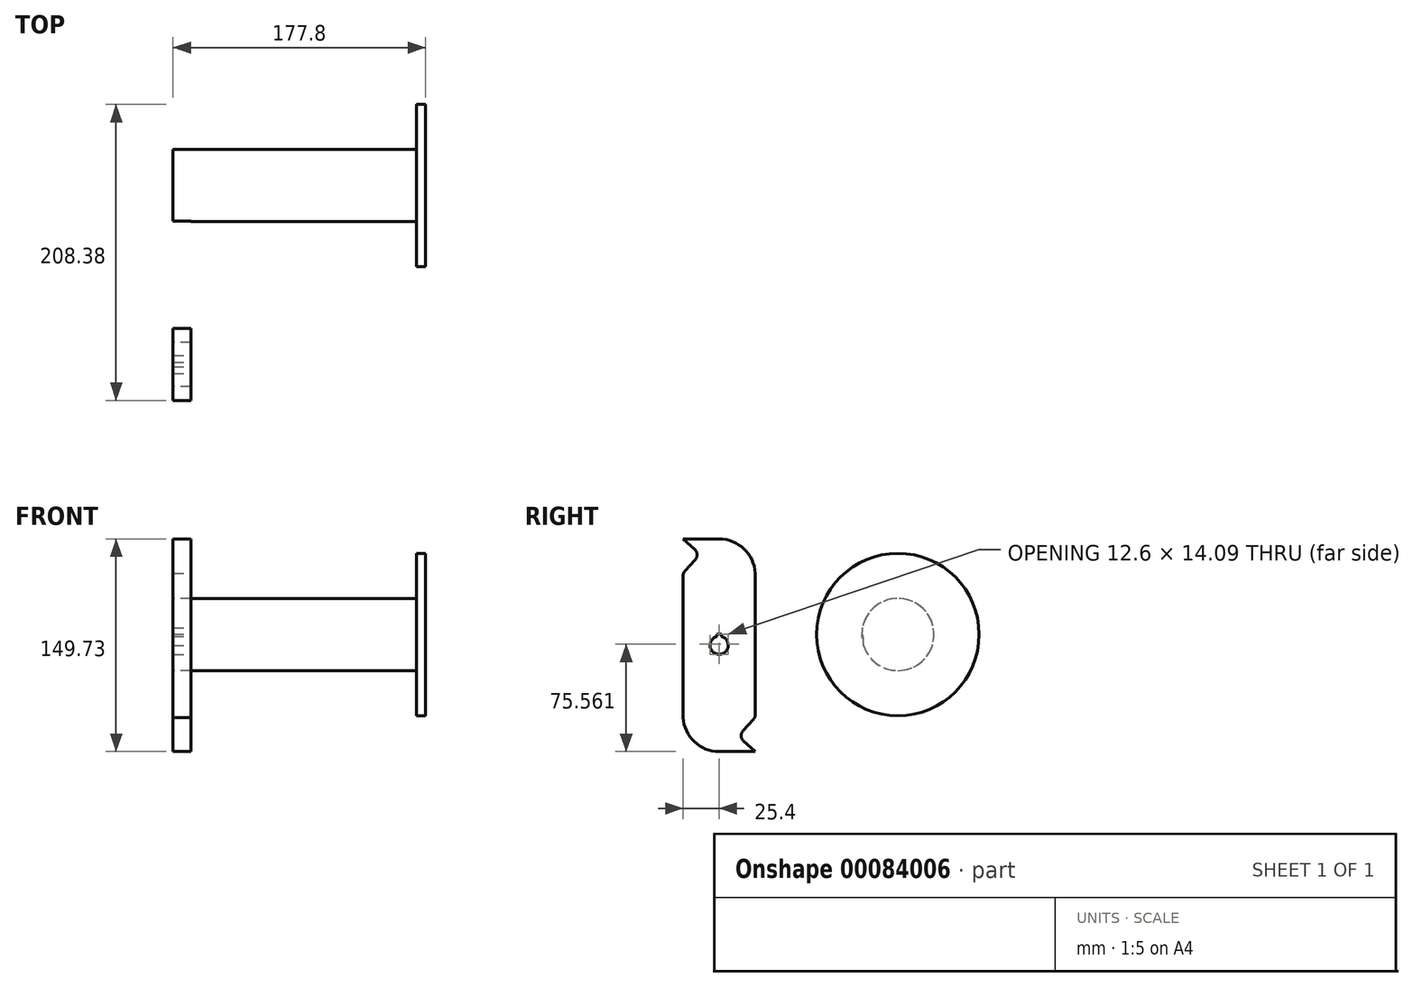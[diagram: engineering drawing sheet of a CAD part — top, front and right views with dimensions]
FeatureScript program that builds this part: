
annotation { "Feature Type Name" : "Feature", "Feature Type Description" : "" }
export const myFeature = defineFeature(function(context is Context, id is Id, definition is map)
    precondition{}
    {
        {
            var Q0;
            Q0=qCreatedBy(makeId("Right.planeOp"),FACE);
            var sketch = newSketch(context, id + "F0", { "sketchPlane" : qUnion([Q0])});
            skCircle(sketch, "E0", {"center": v(0, 0) * mm, "radius": 25.4 * mm});
            skSolve(sketch);
        }
        {
            var Q0;
            Q0=makeQuery(id+"F0.imprint","IMPRINT",FACE,{"disambiguationData":[TD([[makeQuery(id+"F0.imprint","IMPRINT",EDGE,{"derivedFrom":sQuery(id+"F0.wireOp",EDGE,"E0")}),1.0]])]});
            extrude(context, id + "F1", {"entities" : qUnion([Q0]), "depth" : 177.8 * mm});
        }
        {
            var Q0;
            Q0=makeQuery(id+"F1.opExtrude","CAP_FACE",FACE,{"disambiguationData":[OSD([sQuery(id+"F0.wireOp",EDGE,"E0")])],"isStart":false});
            var sketch = newSketch(context, id + "F2", { "sketchPlane" : qUnion([Q0])});
            skCircle(sketch, "E1", {"center": v(0, 0) * mm, "radius": 57.15 * mm});
            skSolve(sketch);
        }
        {
            var Q0;
            Q0=makeQuery(id+"F2.imprint","IMPRINT",FACE,{"disambiguationData":[TD([[makeQuery(id+"F2.imprint","IMPRINT",EDGE,{"derivedFrom":sQuery(id+"F2.wireOp",EDGE,"E1")}),1.0]])]});
            extrude(context, id + "F3", {"entities" : qUnion([Q0]), "operationType" : NewBodyOperationType.ADD, "oppositeDirection" : true, "depth" : 6.35 * mm});
        }
        {
            var Q0;
            Q0=qCreatedBy(makeId("Right.planeOp"),FACE);
            var sketch = newSketch(context, id + "F4", { "sketchPlane" : qUnion([Q0])});
            skCircle(sketch, "E2", {"center": v(-125.83, -7.6) * mm, "radius": 101.6 * mm});
            skSolve(sketch);
        }
        {
            var Q0;
            Q0=makeQuery(id+"F4.imprint","IMPRINT",FACE,{"disambiguationData":[TD([[makeQuery(id+"F4.imprint","IMPRINT",EDGE,{"derivedFrom":sQuery(id+"F4.wireOp",EDGE,"E2")}),1.0]])]});
            extrude(context, id + "F5", {"entities" : qUnion([Q0]), "depth" : 12.7 * mm});
        }
        {
            var Q0;
            Q0=makeQuery(id+"F5.opExtrude","CAP_FACE",FACE,{"disambiguationData":[OSD([sQuery(id+"F4.wireOp",EDGE,"E2")])],"isStart":false});
            var sketch = newSketch(context, id + "F6", { "sketchPlane" : qUnion([Q0])});
            skCircle(sketch, "E3", {"center": v(-125.83, -7.6) * mm, "radius": 6.35 * mm});
            skLineSegment(sketch, "E4", {"start": v(-127.42, -1.45) * mm, "end": v(-127.42, 0.13) * mm});
            skLineSegment(sketch, "E5", {"start": v(-127.42, 0.13) * mm, "end": v(-124.24, 0.13) * mm});
            skLineSegment(sketch, "E6", {"start": v(-124.24, 0.13) * mm, "end": v(-124.24, -1.45) * mm});
            skSolve(sketch);
        }
        {
            var Q0;
            {var subQ0=sQuery(id+"F6.wireOp",EDGE,"E3");var subQ1=makeQuery(id+"F6.imprint","INTERSECT",VERTEX,{"derivedFrom":[subQ0,sQuery(id+"F6.wireOp",EDGE,"E4")]});Q0=makeQuery(id+"F6.imprint","IMPRINT",FACE,{"disambiguationData":[TD([[makeQuery(id+"F6.imprint","IMPRINT",EDGE,{"disambiguationData":[TD([[subQ1,1.0]])],"derivedFrom":subQ0}),1.0]])]});}
            var Q1;
            {var subQ0=sQuery(id+"F6.wireOp",EDGE,"E4");Q1=makeQuery(id+"F6.imprint","IMPRINT",FACE,{"disambiguationData":[TD([[makeQuery(id+"F6.imprint","IMPRINT",EDGE,{"derivedFrom":subQ0}),-1.0]])]});}
            var Q2;
            Q2=makeQuery(id+"F5.opExtrude","CAP_FACE",FACE,{"disambiguationData":[OSD([sQuery(id+"F4.wireOp",EDGE,"E2")])],"isStart":true});
            var Q3;
            Q3=makeQuery(id+"F5.opExtrude","SWEPT_BODY",BODY,{"disambiguationData":[OSD([sQuery(id+"F4.wireOp",EDGE,"E2")])]});
            extrude(context, id + "F7", {"entities" : qUnion([Q0, Q1]), "operationType" : NewBodyOperationType.REMOVE, "endBound" : BoundingType.UP_TO_SURFACE, "oppositeDirection" : true, "endBoundEntityFace" : qUnion([Q2]), "endBoundEntityBody" : qUnion([Q3]), "depth" : 25.4 * mm});
        }
        {
            var Q0;
            Q0=makeQuery(id+"F5.opExtrude","CAP_FACE",FACE,{"disambiguationData":[OSD([sQuery(id+"F4.wireOp",EDGE,"E2")])],"isStart":false});
            var sketch = newSketch(context, id + "F8", { "sketchPlane" : qUnion([Q0])});
            skCircle(sketch, "E7", {"center": v(-125.83, -7.6) * mm, "radius": 25.4 * mm});
            skSolve(sketch);
        }
        {
            var Q0;
            Q0=makeQuery(id+"F8.imprint","IMPRINT",FACE,{"disambiguationData":[TD([[makeQuery(id+"F8.imprint","IMPRINT",EDGE,{"derivedFrom":sQuery(id+"F8.wireOp",EDGE,"E7")}),-1.0]])]});
            var sketch = newSketch(context, id + "F9", { "sketchPlane" : qUnion([Q0])});
            skLineSegment(sketch, "E8", {"start": v(-100.43, 43.2) * mm, "end": v(-100.43, -58.4) * mm});
            skLineSegment(sketch, "E9", {"start": v(-100.43, -58.4) * mm, "end": v(-151.23, -58.4) * mm});
            skLineSegment(sketch, "E10", {"start": v(-151.23, -58.4) * mm, "end": v(-151.23, 43.2) * mm});
            skLineSegment(sketch, "E11", {"start": v(-125.83, 67.26) * mm, "end": v(-151.23, 67.26) * mm});
            skLineSegment(sketch, "E12", {"start": v(-151.23, 67.26) * mm, "end": v(-139.25, 56.38) * mm});
            skLineSegment(sketch, "E13", {"start": v(-139.25, 56.38) * mm, "end": v(-151.23, 43.2) * mm});
            skLineSegment(sketch, "E14", {"start": v(-151.23, 43.2) * mm, "end": v(-100.43, 43.2) * mm});
            skArc(sketch, "E15.MirrorCS", {"start": v(-100.43, 43.2) * mm, "mid": v(-108.34, 60.3) * mm, "end": v(-125.83, 67.26) * mm});
            skLineSegment(sketch, "E16", {"start": v(-90.85, -89.82) * mm, "end": v(-141.65, -89.82) * mm});
            skLineSegment(sketch, "E17", {"start": v(-100.43, -58.4) * mm, "end": v(-112.4, -71.59) * mm});
            skLineSegment(sketch, "E18", {"start": v(-112.4, -71.59) * mm, "end": v(-100.43, -82.47) * mm});
            skLineSegment(sketch, "E19", {"start": v(-100.43, -82.47) * mm, "end": v(-125.83, -82.47) * mm});
            skArc(sketch, "E20", {"start": v(-151.23, -58.4) * mm, "mid": v(-143.32, -75.5) * mm, "end": v(-125.83, -82.47) * mm});
            skLineSegment(sketch, "E21", {"start": v(-151.23, 67.26) * mm, "end": v(-151.23, 43.2) * mm, "construction": true});
            skLineSegment(sketch, "E22", {"start": v(-100.43, -58.4) * mm, "end": v(-100.43, -82.47) * mm, "construction": true});
            skLineSegment(sketch, "E23", {"start": v(-125.83, 67.26) * mm, "end": v(-125.83, -82.47) * mm, "construction": true});
            skLineSegment(sketch, "E24", {"start": v(-116.09, -58.4) * mm, "end": v(-116.09, -82.47) * mm, "construction": true});
            skLineSegment(sketch, "E25", {"start": v(-127.98, 67.26) * mm, "end": v(-127.98, 43.2) * mm, "construction": true});
            skSolve(sketch);
        }
        {
            var Q0;
            Q0=makeQuery(id+"F9.imprint","IMPRINT",FACE,{"disambiguationData":[TD([[makeQuery(id+"F9.imprint","IMPRINT",EDGE,{"derivedFrom":sQuery(id+"F9.wireOp",EDGE,"E11")}),-1.0]])]});
            var Q1;
            Q1=makeQuery(id+"F5.opExtrude","CAP_FACE",FACE,{"disambiguationData":[OSD([sQuery(id+"F4.wireOp",EDGE,"E2")])],"isStart":true});
            extrude(context, id + "F10", {"entities" : qUnion([Q0]), "operationType" : NewBodyOperationType.REMOVE, "endBound" : BoundingType.UP_TO_SURFACE, "oppositeDirection" : true, "endBoundEntityFace" : qUnion([Q1]), "depth" : 25.4 * mm});
        }
        {
            var Q0;
            Q0=makeQuery(id+"F10.boolean.opBoolean","COPY",EDGE,{"derivedFrom":makeQuery(id+"F10.opExtrude","SWEPT_EDGE",EDGE,{"disambiguationData":[OSD([sQuery(id+"F9.wireOp",EDGE,"E10"),sQuery(id+"F9.wireOp",EDGE,"E13"),sQuery(id+"F9.wireOp",EDGE,"E14")])]})});
            var Q1;
            Q1=makeQuery(id+"F10.boolean.opBoolean","COPY",EDGE,{"derivedFrom":makeQuery(id+"F10.opExtrude","SWEPT_EDGE",EDGE,{"disambiguationData":[OSD([sQuery(id+"F9.wireOp",EDGE,"E8"),sQuery(id+"F9.wireOp",EDGE,"E9"),sQuery(id+"F9.wireOp",EDGE,"E17")])]})});
            var Q2;
            Q2=makeQuery(id+"F10.boolean.opBoolean","COPY",EDGE,{"derivedFrom":makeQuery(id+"F10.opExtrude","SWEPT_EDGE",EDGE,{"disambiguationData":[OSD([sQuery(id+"F9.wireOp",EDGE,"E17"),sQuery(id+"F9.wireOp",EDGE,"E18")])]})});
            var Q3;
            Q3=makeQuery(id+"F10.boolean.opBoolean","COPY",EDGE,{"derivedFrom":makeQuery(id+"F10.opExtrude","SWEPT_EDGE",EDGE,{"disambiguationData":[OSD([sQuery(id+"F9.wireOp",EDGE,"E12"),sQuery(id+"F9.wireOp",EDGE,"E13")])]})});
            fillet(context, id + "F11", {"entities" : qUnion([Q0, Q1, Q2, Q3]), "radius" : 5.08 * mm, "tangentPropagation" : true, "allowEdgeOverflow" : false});
        }
    });
